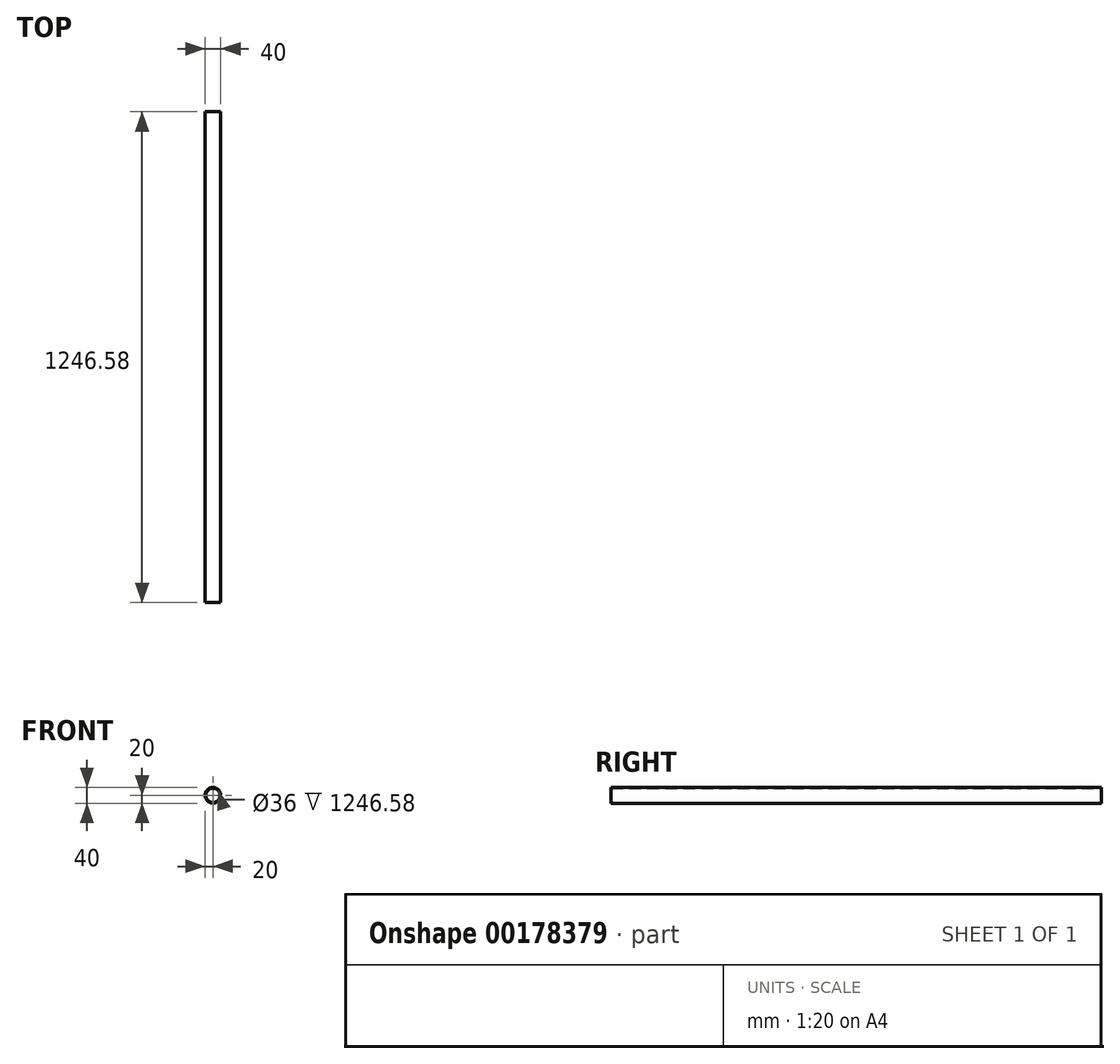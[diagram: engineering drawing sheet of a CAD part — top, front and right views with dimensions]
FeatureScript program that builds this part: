
annotation { "Feature Type Name" : "Feature", "Feature Type Description" : "" }
export const myFeature = defineFeature(function(context is Context, id is Id, definition is map)
    precondition{}
    {
        {
            var Q0;
            Q0=qCreatedBy(makeId("Front.planeOp"),FACE);
            var sketch = newSketch(context, id + "F0", { "sketchPlane" : qUnion([Q0])});
            skCircle(sketch, "E0", {"center": v(0, 0) * mm, "radius": 20 * mm});
            skCircle(sketch, "E1.0", {"center": v(0, 0) * mm, "radius": 18 * mm});
            skSolve(sketch);
        }
        {
            var Q0;
            Q0=makeQuery(id+"F0.imprint","IMPRINT",FACE,{"disambiguationData":[TD([[makeQuery(id+"F0.imprint","IMPRINT",EDGE,{"derivedFrom":sQuery(id+"F0.wireOp",EDGE,"E0")}),1.0]])]});
            extrude(context, id + "F1", {"entities" : qUnion([Q0]), "depth" : 1246.58 * mm});
        }
    });
